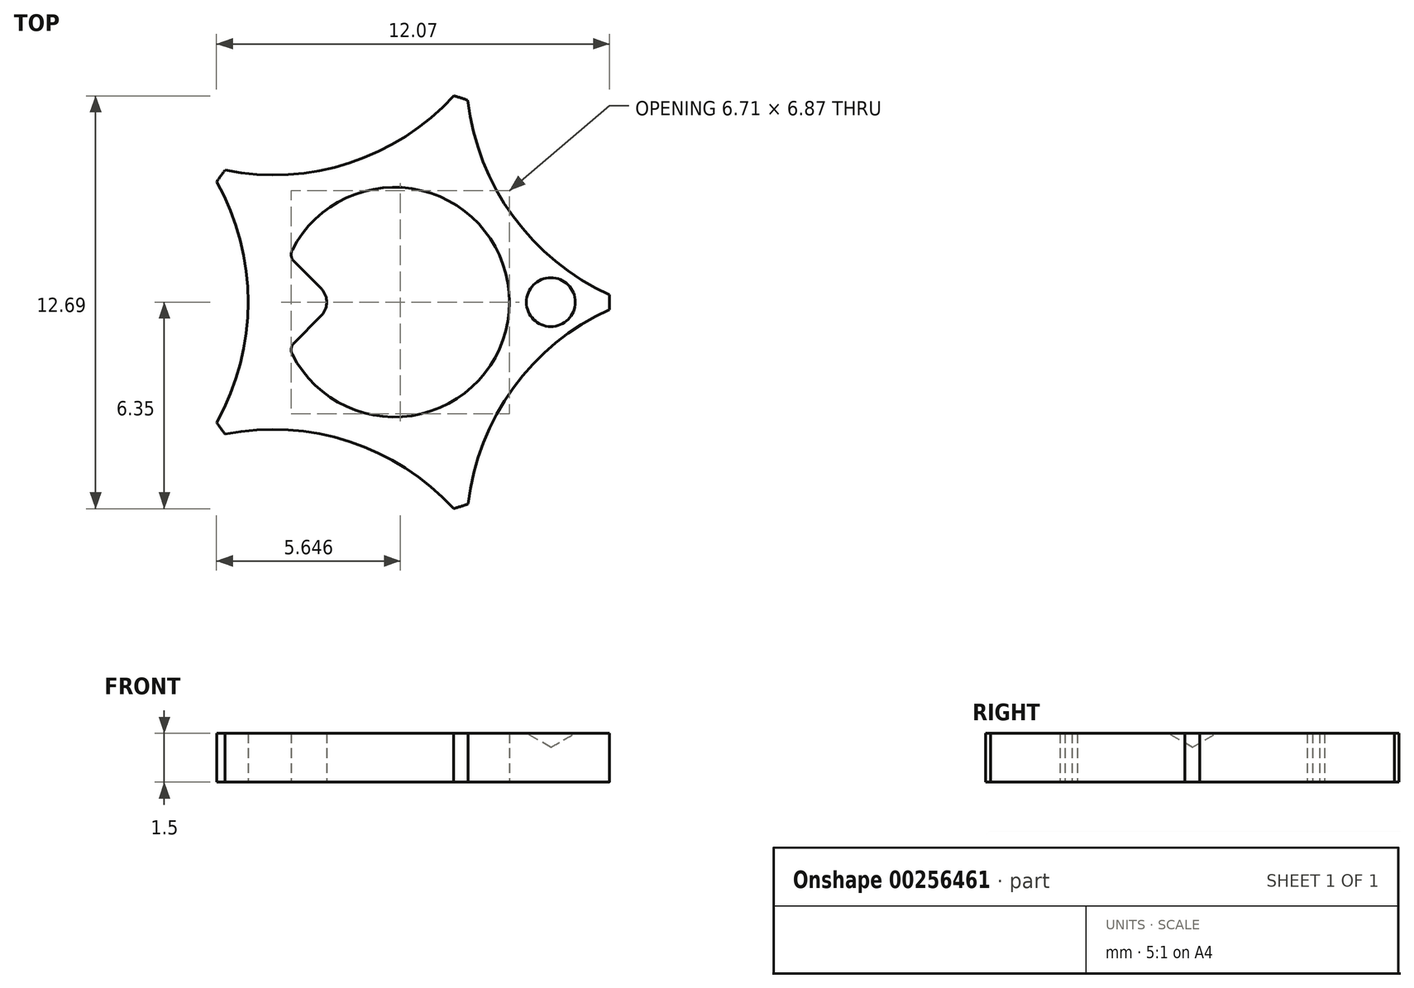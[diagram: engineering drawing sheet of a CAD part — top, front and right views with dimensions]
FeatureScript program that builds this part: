
annotation { "Feature Type Name" : "Feature", "Feature Type Description" : "" }
export const myFeature = defineFeature(function(context is Context, id is Id, definition is map)
    precondition{}
    {
        {
            var Q0;
            Q0=qCreatedBy(makeId("Top.planeOp"),FACE);
            var sketch = newSketch(context, id + "F0", { "sketchPlane" : qUnion([Q0])});
            skArc(sketch, "E0", {"start": v(-1.05, -0.53) * mm, "mid": v(1.18, 0) * mm, "end": v(-1.05, 0.53) * mm});
            skArc(sketch, "E1", {"start": v(-1.73, 1.35) * mm, "mid": v(-1.78, 1.3) * mm, "end": v(-1.82, 1.23) * mm});
            skLineSegment(sketch, "E2", {"start": v(0, 0) * mm, "end": v(2.2, 0) * mm, "construction": true});
            skLineSegment(sketch, "E3", {"start": v(0, 0) * mm, "end": v(0.68, -2.1) * mm, "construction": true});
            skLineSegment(sketch, "E4", {"start": v(0, 0) * mm, "end": v(-1.78, -1.3) * mm, "construction": true});
            skLineSegment(sketch, "E5", {"start": v(0, 0) * mm, "end": v(-1.78, 1.3) * mm, "construction": true});
            skLineSegment(sketch, "E6", {"start": v(0, 0) * mm, "end": v(0.68, 2.1) * mm, "construction": true});
            skPoint(sketch, "E7.third.point", {"position": v(1.22, -0.88) * mm});
            skPoint(sketch, "E8.third.point", {"position": v(-0.74, -1.3) * mm});
            skPoint(sketch, "E9.third.point", {"position": v(-1.5, 0) * mm});
            skPoint(sketch, "E10.third.point", {"position": v(-0.64, 1.3) * mm});
            skPoint(sketch, "E11.third.point", {"position": v(0.97, 1.29) * mm});
            skPoint(sketch, "E12", {"position": v(2.2, 0.08) * mm});
            skPoint(sketch, "E13", {"position": v(2.2, -0.08) * mm});
            skPoint(sketch, "E14", {"position": v(0.75, -2.07) * mm});
            skPoint(sketch, "E15", {"position": v(0.6, -2.12) * mm});
            skPoint(sketch, "E16", {"position": v(-1.73, -1.35) * mm});
            skPoint(sketch, "E17", {"position": v(-1.82, -1.23) * mm});
            skPoint(sketch, "E18", {"position": v(-1.82, 1.23) * mm});
            skPoint(sketch, "E19", {"position": v(-1.73, 1.35) * mm});
            skPoint(sketch, "E20", {"position": v(0.6, 2.11) * mm});
            skPoint(sketch, "E21", {"position": v(0.75, 2.07) * mm});
            skArc(sketch, "E22", {"start": v(2.2, -0.08) * mm, "mid": v(1.21, -0.88) * mm, "end": v(0.75, -2.07) * mm});
            skArc(sketch, "E23", {"start": v(0.6, -2.12) * mm, "mid": v(-0.46, -1.43) * mm, "end": v(-1.73, -1.35) * mm});
            skPoint(sketch, "E23.third.point", {"position": v(-0.74, -1.35) * mm});
            skArc(sketch, "E24", {"start": v(-1.82, -1.23) * mm, "mid": v(-1.5, 0) * mm, "end": v(-1.82, 1.23) * mm});
            skPoint(sketch, "E25.third.point", {"position": v(-0.74, 1.35) * mm});
            skArc(sketch, "E26", {"start": v(0.75, 2.07) * mm, "mid": v(1.21, 0.88) * mm, "end": v(2.2, 0.08) * mm});
            skPoint(sketch, "E27.third.point", {"position": v(-0.39, 1.4) * mm});
            skArc(sketch, "E28", {"start": v(-1.73, 1.35) * mm, "mid": v(-0.46, 1.43) * mm, "end": v(0.6, 2.11) * mm});
            skPoint(sketch, "E29.orphan", {"position": v(-1.93, 1.4) * mm});
            skLineSegment(sketch, "E30", {"start": v(0, 0) * mm, "end": v(-0.61, 0) * mm, "construction": true});
            skLineSegment(sketch, "E31", {"start": v(-0.75, 0.14) * mm, "end": v(-1.03, 0.42) * mm});
            skLineSegment(sketch, "E32", {"start": v(-0.75, -0.14) * mm, "end": v(-1.03, -0.42) * mm});
            skPoint(sketch, "E33.visualSharp", {"position": v(-0.61, 0) * mm});
            skArc(sketch, "E33.filletArc", {"start": v(-0.75, -0.14) * mm, "mid": v(-0.7, 0) * mm, "end": v(-0.75, 0.14) * mm});
            skPoint(sketch, "E34.visualSharp", {"position": v(-1.08, -0.47) * mm});
            skArc(sketch, "E34.filletArc", {"start": v(-1.03, -0.42) * mm, "mid": v(-1.06, -0.47) * mm, "end": v(-1.05, -0.53) * mm});
            skPoint(sketch, "E35.visualSharp", {"position": v(-1.08, 0.47) * mm});
            skArc(sketch, "E35.filletArc", {"start": v(-1.05, 0.53) * mm, "mid": v(-1.06, 0.47) * mm, "end": v(-1.03, 0.42) * mm});
            skArc(sketch, "E36.trimOffspring", {"start": v(0.75, 2.07) * mm, "mid": v(0.68, 2.1) * mm, "end": v(0.6, 2.11) * mm});
            skArc(sketch, "E37.trimOffspring", {"start": v(2.2, -0.08) * mm, "mid": v(2.2, 0) * mm, "end": v(2.2, 0.08) * mm});
            skArc(sketch, "E38.trimOffspring", {"start": v(0.6, -2.12) * mm, "mid": v(0.68, -2.1) * mm, "end": v(0.75, -2.07) * mm});
            skArc(sketch, "E39.trimOffspring", {"start": v(-1.82, -1.23) * mm, "mid": v(-1.78, -1.3) * mm, "end": v(-1.73, -1.35) * mm});
            skSolve(sketch);
        }
        {
            var Q0;
            Q0=makeQuery(id+"F0.imprint","IMPRINT",FACE,{"disambiguationData":[TD([[makeQuery(id+"F0.imprint","IMPRINT",EDGE,{"derivedFrom":sQuery(id+"F0.wireOp",EDGE,"E0")}),-1.0]])]});
            extrude(context, id + "F1", {"entities" : qUnion([Q0]), "depth" : 0.5 * mm});
        }
        {
            var Q0;
            Q0=qCreatedBy(makeId("Front.planeOp"),FACE);
            var sketch = newSketch(context, id + "F2", { "sketchPlane" : qUnion([Q0])});
            skLineSegment(sketch, "E40", {"start": v(0, 0) * mm, "end": v(0, 0.5) * mm, "construction": true});
            skLineSegment(sketch, "E41", {"start": v(0, 0.5) * mm, "end": v(1.6, 0.5) * mm, "construction": true});
            skLineSegment(sketch, "E42", {"start": v(1.6, 0.5) * mm, "end": v(1.85, 0.5) * mm});
            skLineSegment(sketch, "E43", {"start": v(1.6, 0.5) * mm, "end": v(1.35, 0.5) * mm, "construction": true});
            skLineSegment(sketch, "E44", {"start": v(1.85, 0.5) * mm, "end": v(1.6, 0.36) * mm});
            skLineSegment(sketch, "E45", {"start": v(1.6, 0.36) * mm, "end": v(1.35, 0.5) * mm, "construction": true});
            skLineSegment(sketch, "E46", {"start": v(1.6, 0.5) * mm, "end": v(1.6, 0.36) * mm});
            skSolve(sketch);
        }
        {
            var Q0;
            Q0=makeQuery(id+"F2.imprint","IMPRINT",FACE,{"disambiguationData":[TD([[makeQuery(id+"F2.imprint","IMPRINT",EDGE,{"derivedFrom":sQuery(id+"F2.wireOp",EDGE,"E42")}),-1.0]])]});
            var Q1;
            Q1=sQuery(id+"F2.wireOp",EDGE,"E46");
            revolve(context, id + "F3", {"operationType" : NewBodyOperationType.REMOVE, "entities" : qUnion([Q0]), "axis" : qUnion([Q1]), "revolveType" : RevolveType.FULL, "oppositeDirection" : true});
        }
        {
            var Q0;
            Q0=makeQuery(id+"F1.opExtrude","SWEPT_BODY",BODY,{"disambiguationData":[OSD([sQuery(id+"F0.wireOp",EDGE,"E0"),sQuery(id+"F0.wireOp",EDGE,"E1"),sQuery(id+"F0.wireOp",EDGE,"E22"),sQuery(id+"F0.wireOp",EDGE,"E23"),sQuery(id+"F0.wireOp",EDGE,"E24"),sQuery(id+"F0.wireOp",EDGE,"E26"),sQuery(id+"F0.wireOp",EDGE,"E28"),sQuery(id+"F0.wireOp",EDGE,"E31"),sQuery(id+"F0.wireOp",EDGE,"E32"),sQuery(id+"F0.wireOp",EDGE,"E33.filletArc"),sQuery(id+"F0.wireOp",EDGE,"E34.filletArc"),sQuery(id+"F0.wireOp",EDGE,"E35.filletArc"),sQuery(id+"F0.wireOp",EDGE,"E36.trimOffspring"),sQuery(id+"F0.wireOp",EDGE,"E37.trimOffspring"),sQuery(id+"F0.wireOp",EDGE,"E38.trimOffspring"),sQuery(id+"F0.wireOp",EDGE,"E39.trimOffspring")])]});
            var Q1;
            Q1=qCreatedBy(makeId("Origin.pointOp"),VERTEX);
            transform(context, id + "F4", {"entities" : qUnion([Q0]), "transformType" : TransformType.SCALE_UNIFORMLY, "scale" : 3, "makeCopy" : false, "scalePoint" : qUnion([Q1])});
        }
    });
